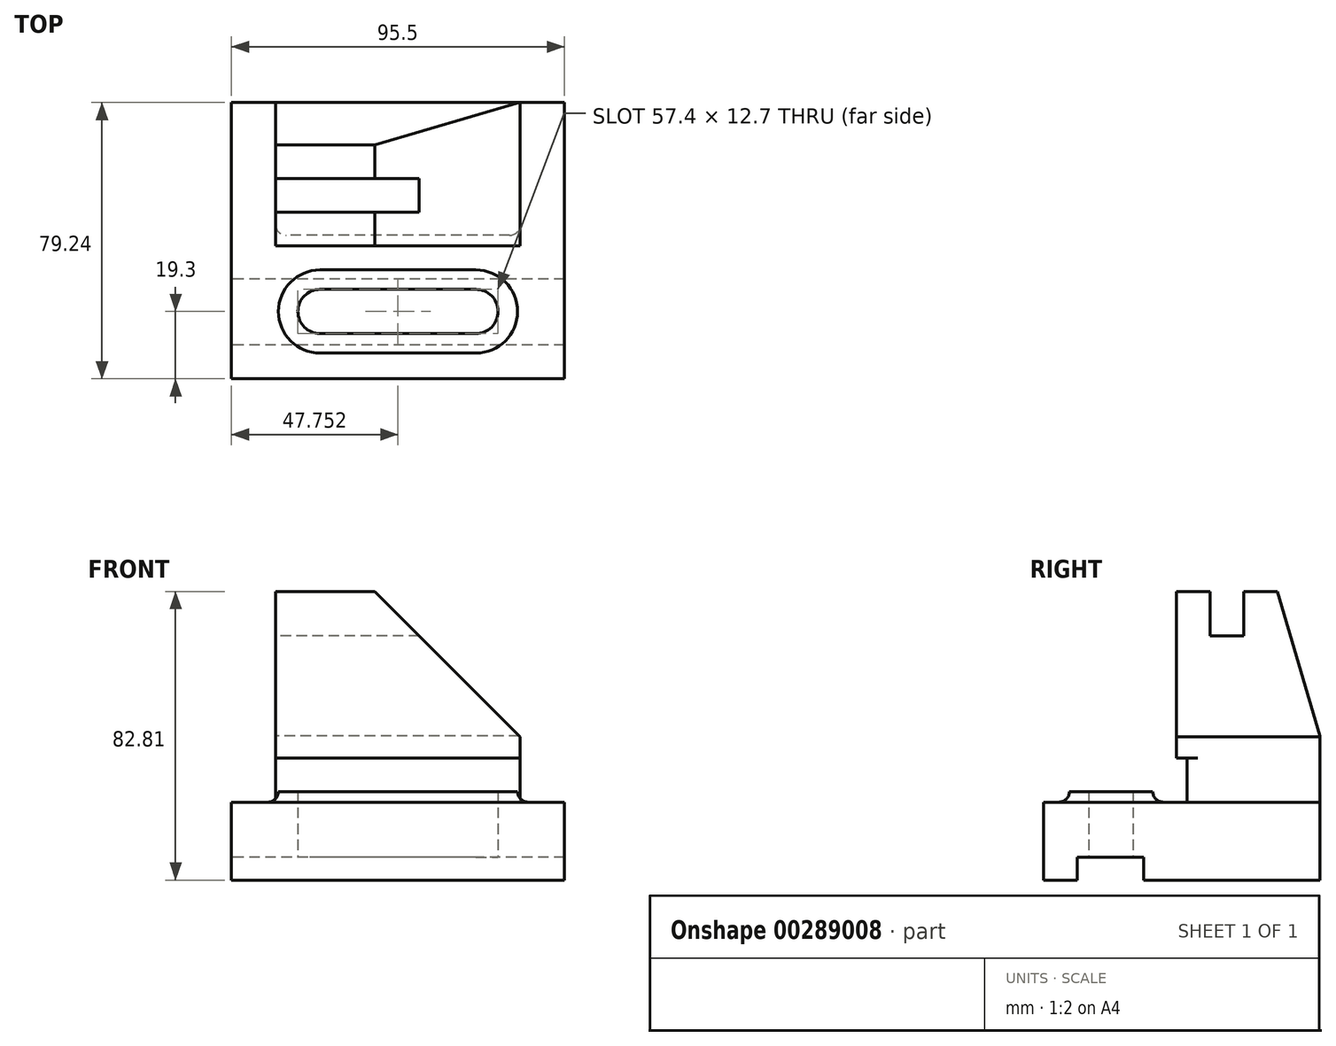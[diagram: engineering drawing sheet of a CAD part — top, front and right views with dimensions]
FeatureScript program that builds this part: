
annotation { "Feature Type Name" : "Feature", "Feature Type Description" : "" }
export const myFeature = defineFeature(function(context is Context, id is Id, definition is map)
    precondition{}
    {
        {
            var Q0;
            Q0=qCreatedBy(makeId("Right.planeOp"),FACE);
            var sketch = newSketch(context, id + "F0", { "sketchPlane" : qUnion([Q0])});
            skLineSegment(sketch, "E0.rect.bottom", {"start": v(39.62, 11.18) * mm, "end": v(-39.62, 11.18) * mm});
            skLineSegment(sketch, "E0.rect.top", {"start": v(39.62, -11.18) * mm, "end": v(-39.62, -11.18) * mm});
            skLineSegment(sketch, "E0.rect.left", {"start": v(39.62, 11.18) * mm, "end": v(39.62, -11.18) * mm});
            skLineSegment(sketch, "E0.rect.right", {"start": v(-39.62, 11.18) * mm, "end": v(-39.62, -11.18) * mm});
            skPoint(sketch, "E0.rect.middle", {"position": v(0, 0) * mm});
            skLineSegment(sketch, "E1.bottom", {"start": v(-29.97, -11.18) * mm, "end": v(-11, -11.18) * mm});
            skLineSegment(sketch, "E1.top", {"start": v(-29.97, -4.57) * mm, "end": v(-11, -4.57) * mm});
            skLineSegment(sketch, "E1.left", {"start": v(-29.97, -11.18) * mm, "end": v(-29.97, -4.57) * mm});
            skLineSegment(sketch, "E1.right", {"start": v(-11, -11.18) * mm, "end": v(-11, -4.57) * mm});
            skSolve(sketch);
        }
        {
            var Q0;
            Q0=makeQuery(id+"F0.imprint","IMPRINT",FACE,{"disambiguationData":[TD([[makeQuery(id+"F0.imprint","IMPRINT",EDGE,{"derivedFrom":sQuery(id+"F0.wireOp",EDGE,"E0.rect.bottom")}),1.0]])]});
            extrude(context, id + "F1", {"entities" : qUnion([Q0]), "depth" : 95.5 * mm});
        }
        {
            var Q0;
            Q0=makeQuery(id+"F1.opExtrude","SWEPT_FACE",FACE,{"disambiguationData":[OSD([sQuery(id+"F0.wireOp",EDGE,"E0.rect.bottom")])]});
            var sketch = newSketch(context, id + "F2", { "sketchPlane" : qUnion([Q0])});
            skCircle(sketch, "E2", {"center": v(25.4, -20.32) * mm, "radius": 6.35 * mm});
            skCircle(sketch, "E3", {"center": v(25.4, -20.32) * mm, "radius": 11.94 * mm});
            skCircle(sketch, "E4", {"center": v(70.1, -20.32) * mm, "radius": 6.35 * mm});
            skCircle(sketch, "E5", {"center": v(70.1, -20.32) * mm, "radius": 11.94 * mm});
            skLineSegment(sketch, "E6", {"start": v(70.1, -32.26) * mm, "end": v(25.4, -32.26) * mm});
            skLineSegment(sketch, "E7", {"start": v(25.4, -8.38) * mm, "end": v(70.1, -8.38) * mm});
            skLineSegment(sketch, "E8", {"start": v(70.1, -13.97) * mm, "end": v(25.4, -13.97) * mm});
            skLineSegment(sketch, "E9", {"start": v(25.4, -26.67) * mm, "end": v(70.1, -26.67) * mm});
            skSolve(sketch);
        }
        {
            var Q0;
            Q0=qSketchRegion(id+"F2",true);
            extrude(context, id + "F3", {"entities" : qUnion([Q0]), "operationType" : NewBodyOperationType.ADD, "depth" : 3.05 * mm});
        }
        {
            var Q0;
            {var subQ0=sQuery(id+"F2.wireOp",EDGE,"E2");var subQ2=makeQuery(id+"F2.imprint","INTERSECT",VERTEX,{"derivedFrom":[subQ0,sQuery(id+"F2.wireOp",EDGE,"E8")]});Q0=makeQuery(id+"F2.imprint","IMPRINT",FACE,{"disambiguationData":[TD([[makeQuery(id+"F2.imprint","IMPRINT",EDGE,{"disambiguationData":[TD([[subQ2,-1.0]])],"derivedFrom":subQ0}),1.0]])]});}
            var Q1;
            {var subQ3=sQuery(id+"F2.wireOp",EDGE,"E2");var subQ5=sQuery(id+"F2.wireOp",EDGE,"E8");var subQ7=makeQuery(id+"F2.imprint","INTERSECT",VERTEX,{"derivedFrom":[subQ3,subQ5]});Q1=makeQuery(id+"F2.imprint","IMPRINT",FACE,{"disambiguationData":[TD([[makeQuery(id+"F2.imprint","IMPRINT",EDGE,{"disambiguationData":[TD([[subQ7,1.0]])],"derivedFrom":subQ3}),-1.0]])]});}
            var Q2;
            {var subQ3=sQuery(id+"F2.wireOp",EDGE,"E3");var subQ5=sQuery(id+"F2.wireOp",EDGE,"E8");var subQ7=makeQuery(id+"F2.imprint","INTERSECT",VERTEX,{"derivedFrom":[subQ3,subQ5]});Q2=makeQuery(id+"F2.imprint","IMPRINT",FACE,{"disambiguationData":[TD([[makeQuery(id+"F2.imprint","IMPRINT",EDGE,{"disambiguationData":[TD([[subQ7,1.0]])],"derivedFrom":subQ3}),-1.0]])]});}
            var Q3;
            {var subQ3=sQuery(id+"F2.wireOp",EDGE,"E4");var subQ5=sQuery(id+"F2.wireOp",EDGE,"E8");var subQ7=makeQuery(id+"F2.imprint","INTERSECT",VERTEX,{"derivedFrom":[subQ3,subQ5]});Q3=makeQuery(id+"F2.imprint","IMPRINT",FACE,{"disambiguationData":[TD([[makeQuery(id+"F2.imprint","IMPRINT",EDGE,{"disambiguationData":[TD([[subQ7,-1.0]])],"derivedFrom":subQ3}),-1.0]])]});}
            var Q4;
            {var subQ0=sQuery(id+"F2.wireOp",EDGE,"E4");var subQ2=makeQuery(id+"F2.imprint","INTERSECT",VERTEX,{"derivedFrom":[subQ0,sQuery(id+"F2.wireOp",EDGE,"E8")]});Q4=makeQuery(id+"F2.imprint","IMPRINT",FACE,{"disambiguationData":[TD([[makeQuery(id+"F2.imprint","IMPRINT",EDGE,{"disambiguationData":[TD([[subQ2,-1.0]])],"derivedFrom":subQ0}),1.0]])]});}
            extrude(context, id + "F4", {"entities" : qUnion([Q0, Q1, Q2, Q3, Q4]), "operationType" : NewBodyOperationType.REMOVE, "endBound" : BoundingType.THROUGH_ALL, "oppositeDirection" : true, "depth" : 25.4 * mm});
        }
        {
            var Q0;
            Q0=makeQuery(id+"F1.opExtrude","SWEPT_FACE",FACE,{"disambiguationData":[OSD([sQuery(id+"F0.wireOp",EDGE,"E0.rect.left")])]});
            var sketch = newSketch(context, id + "F5", { "sketchPlane" : qUnion([Q0])});
            skLineSegment(sketch, "E10.bottom", {"start": v(-82.8, 11.18) * mm, "end": v(-12.7, 11.18) * mm});
            skLineSegment(sketch, "E10.top", {"start": v(-82.8, 71.63) * mm, "end": v(-12.7, 71.63) * mm});
            skLineSegment(sketch, "E10.left", {"start": v(-82.8, 11.18) * mm, "end": v(-82.8, 71.63) * mm});
            skLineSegment(sketch, "E10.right", {"start": v(-12.7, 11.18) * mm, "end": v(-12.7, 71.63) * mm});
            skLineSegment(sketch, "E11", {"start": v(-82.8, 29.97) * mm, "end": v(-41.15, 71.63) * mm});
            skLineSegment(sketch, "E12", {"start": v(-82.8, 23.88) * mm, "end": v(-12.7, 23.88) * mm});
            skSolve(sketch);
        }
        {
            var Q0;
            {var subQ0=sQuery(id+"F5.wireOp",EDGE,"E11");Q0=makeQuery(id+"F5.imprint","IMPRINT",FACE,{"disambiguationData":[TD([[makeQuery(id+"F5.imprint","IMPRINT",EDGE,{"derivedFrom":subQ0}),-1.0]])]});}
            extrude(context, id + "F6", {"entities" : qUnion([Q0]), "oppositeDirection" : true, "depth" : 41.15 * mm});
        }
        {
            var Q0;
            {var subQ3=sQuery(id+"F5.wireOp",EDGE,"E10.bottom");Q0=makeQuery(id+"F5.imprint","IMPRINT",FACE,{"disambiguationData":[TD([[makeQuery(id+"F5.imprint","IMPRINT",EDGE,{"derivedFrom":subQ3}),1.0]])]});}
            extrude(context, id + "F7", {"entities" : qUnion([Q0]), "operationType" : NewBodyOperationType.ADD, "oppositeDirection" : true, "depth" : 38.1 * mm});
        }
        {
            var Q0;
            {var subQ0=sQuery(id+"F5.wireOp",EDGE,"E10.right");Q0=makeQuery(id+"F7.boolean.opBoolean","MERGE",FACE,{"derivedFrom":[makeQuery(id+"F6.opExtrude","SWEPT_FACE",FACE,{"disambiguationData":[OSD([subQ0])]}),makeQuery(id+"F7.opExtrude","SWEPT_FACE",FACE,{"disambiguationData":[OSD([subQ0])]})]});}
            var sketch = newSketch(context, id + "F8", { "sketchPlane" : qUnion([Q0])});
            skLineSegment(sketch, "E13", {"start": v(-39.62, 30.15) * mm, "end": v(-27.43, 71.63) * mm});
            skLineSegment(sketch, "E14.bottom", {"start": v(-17.78, 71.63) * mm, "end": v(-8.13, 71.63) * mm});
            skLineSegment(sketch, "E14.top", {"start": v(-17.78, 58.93) * mm, "end": v(-8.13, 58.93) * mm});
            skLineSegment(sketch, "E14.left", {"start": v(-17.78, 71.63) * mm, "end": v(-17.78, 58.93) * mm});
            skLineSegment(sketch, "E14.right", {"start": v(-8.13, 71.63) * mm, "end": v(-8.13, 58.93) * mm});
            skSolve(sketch);
        }
        {
            var Q0;
            {var subQ2=sQuery(id+"F8.wireOp",EDGE,"E13");Q0=makeQuery(id+"F8.imprint","IMPRINT",FACE,{"disambiguationData":[TD([[makeQuery(id+"F8.imprint","IMPRINT",EDGE,{"derivedFrom":subQ2}),1.0]])]});}
            var Q1;
            Q1=makeQuery(id+"F8.imprint","IMPRINT",FACE,{"disambiguationData":[TD([[makeQuery(id+"F8.imprint","IMPRINT",EDGE,{"derivedFrom":sQuery(id+"F8.wireOp",EDGE,"E14.bottom")}),1.0]])]});
            extrude(context, id + "F9", {"entities" : qUnion([Q0, Q1]), "operationType" : NewBodyOperationType.REMOVE, "endBound" : BoundingType.THROUGH_ALL, "oppositeDirection" : true, "depth" : 25.4 * mm});
        }
        {
            var Q0;
            Q0=makeQuery(id+"F7.opExtrude","CAP_EDGE",EDGE,{"disambiguationData":[OSD([sQuery(id+"F5.wireOp",EDGE,"E10.bottom")])],"isStart":false});
            var Q1;
            Q1=makeQuery(id+"F7.opExtrude","CAP_EDGE",EDGE,{"disambiguationData":[OSD([sQuery(id+"F5.wireOp",EDGE,"E10.left")])],"isStart":false});
            var Q2;
            Q2=makeQuery(id+"F7.opExtrude","CAP_EDGE",EDGE,{"disambiguationData":[OSD([sQuery(id+"F5.wireOp",EDGE,"E12")])],"isStart":false});
            var Q3;
            Q3=makeQuery(id+"F7.opExtrude","CAP_EDGE",EDGE,{"disambiguationData":[OSD([sQuery(id+"F5.wireOp",EDGE,"E10.right")])],"isStart":false});
            var Q4;
            Q4=makeQuery(id+"F7.opExtrude","SWEPT_EDGE",EDGE,{"disambiguationData":[OSD([sQuery(id+"F0.wireOp",EDGE,"E0.rect.bottom"),sQuery(id+"F0.wireOp",EDGE,"E0.rect.left"),sQuery(id+"F5.wireOp",EDGE,"E10.bottom"),sQuery(id+"F5.wireOp",EDGE,"E10.right")])]});
            var Q5;
            Q5=makeQuery(id+"F3.opExtrude","CAP_EDGE",EDGE,{"disambiguationData":[OSD([sQuery(id+"F2.wireOp",EDGE,"E6")])],"isStart":true});
            fillet(context, id + "F10", {"entities" : qUnion([Q0, Q1, Q2, Q3, Q4, Q5]), "radius" : 3.05 * mm, "tangentPropagation" : true, "allowEdgeOverflow" : false});
        }
    });
